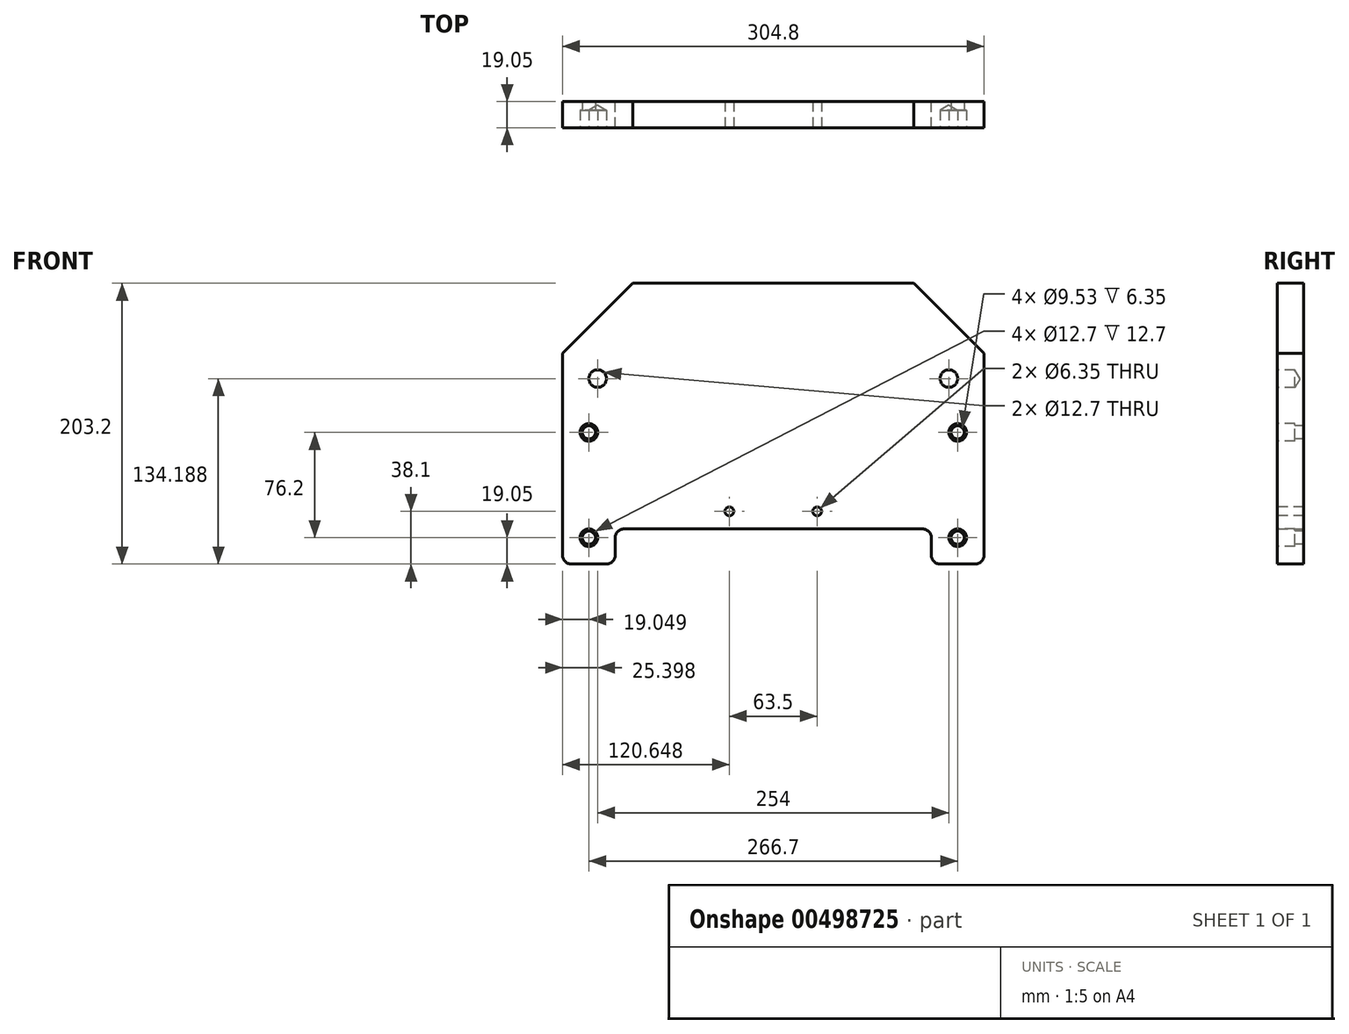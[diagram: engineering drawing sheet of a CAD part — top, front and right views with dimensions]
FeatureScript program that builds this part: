
annotation { "Feature Type Name" : "Feature", "Feature Type Description" : "" }
export const myFeature = defineFeature(function(context is Context, id is Id, definition is map)
    precondition{}
    {
        {
            var Q0;
            Q0=qCreatedBy(makeId("Front.planeOp"),FACE);
            var sketch = newSketch(context, id + "F0", { "sketchPlane" : qUnion([Q0])});
            skLineSegment(sketch, "E0", {"start": v(-61.53, -19.05) * mm, "end": v(-23.43, -19.05) * mm});
            skLineSegment(sketch, "E1", {"start": v(-23.43, -19.05) * mm, "end": v(-23.43, 6.35) * mm});
            skLineSegment(sketch, "E2", {"start": v(-23.43, 6.35) * mm, "end": v(205.17, 6.35) * mm});
            skLineSegment(sketch, "E3", {"start": v(205.17, 6.35) * mm, "end": v(205.17, -19.05) * mm});
            skLineSegment(sketch, "E4", {"start": v(205.17, -19.05) * mm, "end": v(243.27, -19.05) * mm});
            skLineSegment(sketch, "E5", {"start": v(243.27, -19.05) * mm, "end": v(243.27, 184.15) * mm});
            skLineSegment(sketch, "E6", {"start": v(243.27, 184.15) * mm, "end": v(-61.53, 184.15) * mm});
            skLineSegment(sketch, "E7", {"start": v(-61.53, 184.15) * mm, "end": v(-61.53, -19.05) * mm});
            skSolve(sketch);
        }
        {
            var Q0;
            Q0=qSketchRegion(id+"F0",true);
            extrude(context, id + "F1", {"entities" : qUnion([Q0]), "depth" : 19.05 * mm});
        }
        {
            var Q0;
            Q0=makeQuery(id+"F1.opExtrude","SWEPT_EDGE",EDGE,{"disambiguationData":[OSD([sQuery(id+"F0.wireOp",EDGE,"E1"),sQuery(id+"F0.wireOp",EDGE,"E2")])]});
            var Q1;
            Q1=makeQuery(id+"F1.opExtrude","SWEPT_EDGE",EDGE,{"disambiguationData":[OSD([sQuery(id+"F0.wireOp",EDGE,"E0"),sQuery(id+"F0.wireOp",EDGE,"E7")])]});
            var Q2;
            Q2=makeQuery(id+"F1.opExtrude","SWEPT_EDGE",EDGE,{"disambiguationData":[OSD([sQuery(id+"F0.wireOp",EDGE,"E4"),sQuery(id+"F0.wireOp",EDGE,"E5")])]});
            var Q3;
            Q3=makeQuery(id+"F1.opExtrude","SWEPT_EDGE",EDGE,{"disambiguationData":[OSD([sQuery(id+"F0.wireOp",EDGE,"E3"),sQuery(id+"F0.wireOp",EDGE,"E4")])]});
            var Q4;
            Q4=makeQuery(id+"F1.opExtrude","SWEPT_EDGE",EDGE,{"disambiguationData":[OSD([sQuery(id+"F0.wireOp",EDGE,"E2"),sQuery(id+"F0.wireOp",EDGE,"E3")])]});
            var Q5;
            Q5=makeQuery(id+"F1.opExtrude","SWEPT_EDGE",EDGE,{"disambiguationData":[OSD([sQuery(id+"F0.wireOp",EDGE,"E0"),sQuery(id+"F0.wireOp",EDGE,"E1")])]});
            fillet(context, id + "F2", {"entities" : qUnion([Q0, Q1, Q2, Q3, Q4, Q5]), "radius" : 6.35 * mm, "tangentPropagation" : true, "allowEdgeOverflow" : false});
        }
        {
            var Q0;
            Q0=makeQuery(id+"F1.opExtrude","SWEPT_EDGE",EDGE,{"disambiguationData":[OSD([sQuery(id+"F0.wireOp",EDGE,"E5"),sQuery(id+"F0.wireOp",EDGE,"E6")])]});
            var Q1;
            Q1=makeQuery(id+"F1.opExtrude","SWEPT_EDGE",EDGE,{"disambiguationData":[OSD([sQuery(id+"F0.wireOp",EDGE,"E6"),sQuery(id+"F0.wireOp",EDGE,"E7")])]});
            chamfer(context, id + "F3", {"entities" : qUnion([Q0, Q1]), "chamferType" : ChamferType.OFFSET_ANGLE, "width" : 50.8 * mm, "oppositeDirection" : false, "angle" : 45 * degree, "tangentPropagation" : true});
        }
        {
            var Q0;
            Q0=makeQuery(id+"F1.opExtrude","CAP_FACE",FACE,{"disambiguationData":[OSD([sQuery(id+"F0.wireOp",EDGE,"E0"),sQuery(id+"F0.wireOp",EDGE,"E1"),sQuery(id+"F0.wireOp",EDGE,"E2"),sQuery(id+"F0.wireOp",EDGE,"E3"),sQuery(id+"F0.wireOp",EDGE,"E4"),sQuery(id+"F0.wireOp",EDGE,"E5"),sQuery(id+"F0.wireOp",EDGE,"E6"),sQuery(id+"F0.wireOp",EDGE,"E7")])],"isStart":false});
            var sketch = newSketch(context, id + "F4", { "sketchPlane" : qUnion([Q0])});
            skCircle(sketch, "E8", {"center": v(217.87, 115.14) * mm, "radius": 6.35 * mm});
            skCircle(sketch, "E9", {"center": v(-36.13, 115.14) * mm, "radius": 6.35 * mm});
            skCircle(sketch, "E10", {"center": v(59.12, 19.05) * mm, "radius": 3.18 * mm});
            skCircle(sketch, "E11", {"center": v(122.62, 19.05) * mm, "radius": 3.17 * mm});
            skCircle(sketch, "E12", {"center": v(-42.48, 0) * mm, "radius": 6.35 * mm});
            skCircle(sketch, "E13", {"center": v(-42.48, 76.2) * mm, "radius": 6.35 * mm});
            skCircle(sketch, "E14", {"center": v(224.22, 76.2) * mm, "radius": 6.35 * mm});
            skCircle(sketch, "E15", {"center": v(224.22, 0) * mm, "radius": 6.35 * mm});
            skSolve(sketch);
        }
        {
            var Q0;
            Q0=makeQuery(id+"F4.imprint","IMPRINT",FACE,{"disambiguationData":[TD([[makeQuery(id+"F4.imprint","IMPRINT",EDGE,{"derivedFrom":sQuery(id+"F4.wireOp",EDGE,"XaNgVts7-AhXR-bNit-7f5S-FPTi6G3fDlpo")}),1.0]])]});
            var Q1;
            Q1=makeQuery(id+"F4.imprint","IMPRINT",FACE,{"disambiguationData":[TD([[makeQuery(id+"F4.imprint","IMPRINT",EDGE,{"derivedFrom":sQuery(id+"F4.wireOp",EDGE,"E10")}),1.0]])]});
            var Q2;
            Q2=makeQuery(id+"F4.imprint","IMPRINT",FACE,{"disambiguationData":[TD([[makeQuery(id+"F4.imprint","IMPRINT",EDGE,{"derivedFrom":sQuery(id+"F4.wireOp",EDGE,"E11")}),1.0]])]});
            extrude(context, id + "F5", {"entities" : qUnion([Q0, Q1, Q2]), "operationType" : NewBodyOperationType.REMOVE, "oppositeDirection" : true, "depth" : 25.4 * mm});
        }
        {
            var Q0;
            Q0=sQuery(id+"F4.wireOp",VERTEX,"E9.center");
            var Q1;
            Q1=sQuery(id+"F4.wireOp",VERTEX,"E8.center");
            var Q2;
            Q2=makeQuery(id+"F1.opExtrude","SWEPT_BODY",BODY,{"disambiguationData":[OSD([sQuery(id+"F0.wireOp",EDGE,"E0"),sQuery(id+"F0.wireOp",EDGE,"E1"),sQuery(id+"F0.wireOp",EDGE,"E2"),sQuery(id+"F0.wireOp",EDGE,"E3"),sQuery(id+"F0.wireOp",EDGE,"E4"),sQuery(id+"F0.wireOp",EDGE,"E5"),sQuery(id+"F0.wireOp",EDGE,"E6"),sQuery(id+"F0.wireOp",EDGE,"E7")])]});
            hole(context, id + "F6", {"style" : HoleStyle.SIMPLE, "endStyle" : HoleEndStyle.BLIND, "holeDiameter" : 12.7 * mm, "holeDepth" : 12.7 * mm, "tappedDepth" : 12.7 * mm, "tapClearance" : 3, "startFromSketch" : true, "locations" : qUnion([Q0, Q1]), "scope" : qUnion([Q2])});
        }
        {
            var Q0;
            Q0=sQuery(id+"F4.wireOp",VERTEX,"E13.center");
            var Q1;
            Q1=sQuery(id+"F4.wireOp",VERTEX,"E12.center");
            var Q2;
            Q2=sQuery(id+"F4.wireOp",VERTEX,"E15.center");
            var Q3;
            Q3=sQuery(id+"F4.wireOp",VERTEX,"E14.center");
            var Q4;
            Q4=makeQuery(id+"F1.opExtrude","SWEPT_BODY",BODY,{"disambiguationData":[OSD([sQuery(id+"F0.wireOp",EDGE,"E0"),sQuery(id+"F0.wireOp",EDGE,"E1"),sQuery(id+"F0.wireOp",EDGE,"E2"),sQuery(id+"F0.wireOp",EDGE,"E3"),sQuery(id+"F0.wireOp",EDGE,"E4"),sQuery(id+"F0.wireOp",EDGE,"E5"),sQuery(id+"F0.wireOp",EDGE,"E6"),sQuery(id+"F0.wireOp",EDGE,"E7")])]});
            hole(context, id + "F7", {"style" : HoleStyle.C_BORE, "endStyle" : HoleEndStyle.BLIND, "holeDiameter" : 9.52 * mm, "cBoreDiameter" : 12.7 * mm, "cBoreDepth" : 12.7 * mm, "holeDepth" : 25.4 * mm, "tappedDepth" : 12.7 * mm, "tapClearance" : 3, "startFromSketch" : true, "locations" : qUnion([Q0, Q1, Q2, Q3]), "scope" : qUnion([Q4])});
        }
    });
